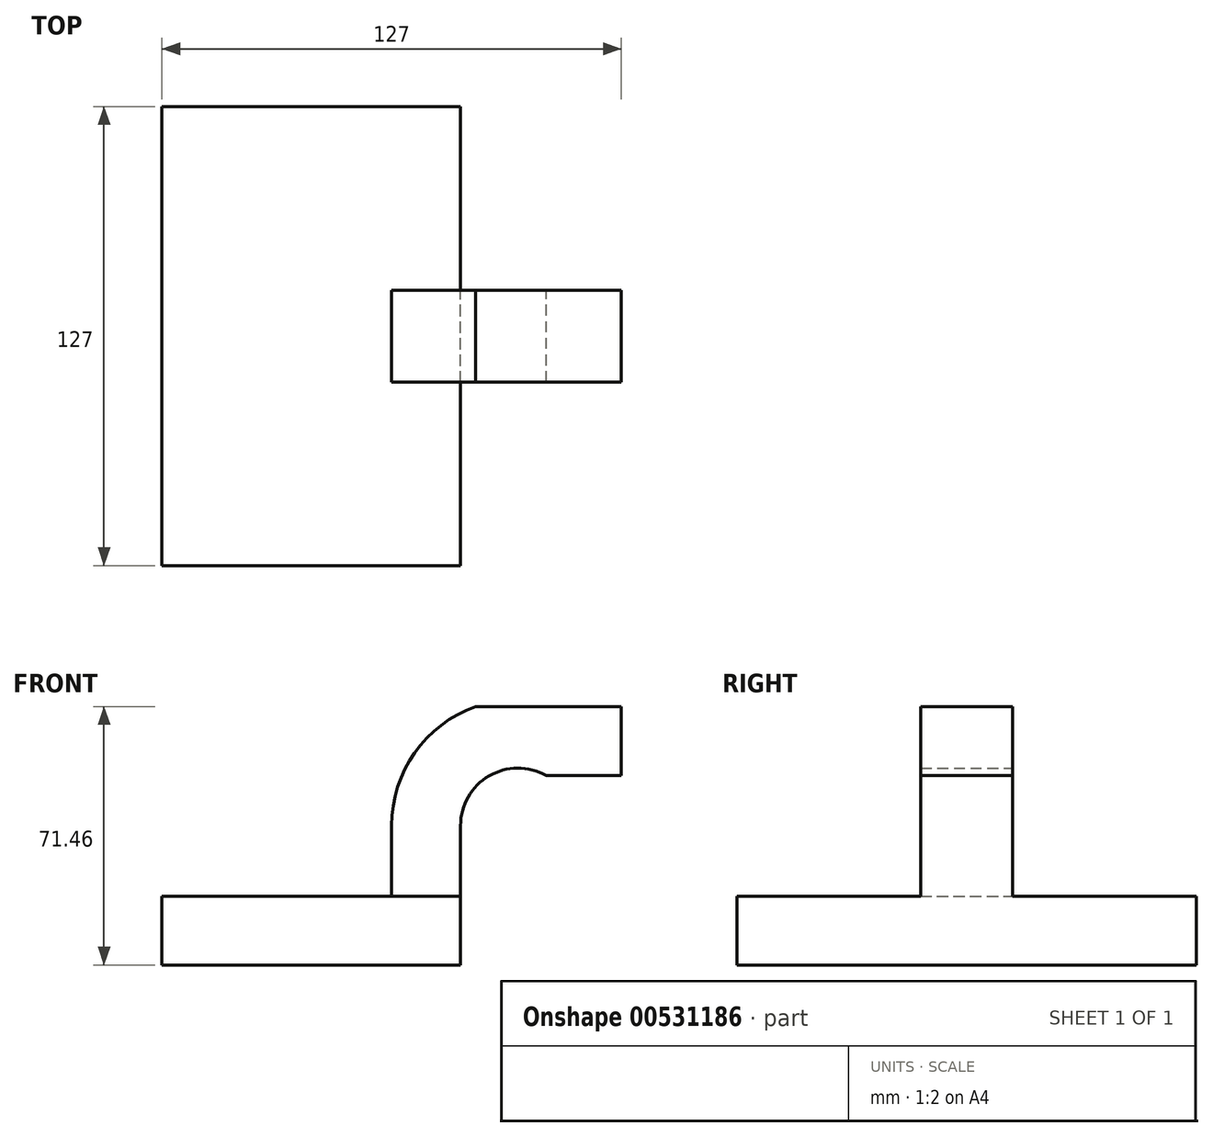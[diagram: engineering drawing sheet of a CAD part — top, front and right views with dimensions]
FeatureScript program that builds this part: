
annotation { "Feature Type Name" : "Feature", "Feature Type Description" : "" }
export const myFeature = defineFeature(function(context is Context, id is Id, definition is map)
    precondition{}
    {
        {
            var Q0;
            Q0=qCreatedBy(makeId("Front.planeOp"),FACE);
            var sketch = newSketch(context, id + "F0", { "sketchPlane" : qUnion([Q0])});
            skLineSegment(sketch, "E0.bottom", {"start": v(-41.28, -9.53) * mm, "end": v(41.28, -9.53) * mm});
            skLineSegment(sketch, "E0.top", {"start": v(-41.28, 9.53) * mm, "end": v(41.28, 9.53) * mm});
            skLineSegment(sketch, "E0.left", {"start": v(-41.28, -9.53) * mm, "end": v(-41.28, 9.53) * mm});
            skLineSegment(sketch, "E0.right", {"start": v(41.28, -9.53) * mm, "end": v(41.28, 9.53) * mm});
            skPoint(sketch, "E0.middle", {"position": v(0, 0) * mm});
            skLineSegment(sketch, "E1.bottom", {"start": v(111.12, 38.1) * mm, "end": v(60.32, 38.1) * mm});
            skLineSegment(sketch, "E1.top", {"start": v(111.12, 66.68) * mm, "end": v(60.32, 66.68) * mm});
            skLineSegment(sketch, "E1.left", {"start": v(111.12, 38.1) * mm, "end": v(111.12, 66.68) * mm});
            skLineSegment(sketch, "E1.right", {"start": v(60.32, 38.1) * mm, "end": v(60.32, 66.68) * mm});
            skPoint(sketch, "E1.middle", {"position": v(85.72, 52.39) * mm});
            skLineSegment(sketch, "E2", {"start": v(41.28, 9.53) * mm, "end": v(41.28, 29.04) * mm});
            skArc(sketch, "E3", {"start": v(41.28, 29.04) * mm, "mid": v(49.14, 42.75) * mm, "end": v(64.94, 42.88) * mm});
            skLineSegment(sketch, "E4", {"start": v(64.94, 42.88) * mm, "end": v(85.72, 42.88) * mm});
            skLineSegment(sketch, "E5.0", {"start": v(45.38, 61.93) * mm, "end": v(85.72, 61.93) * mm});
            skArc(sketch, "E5.1", {"start": v(22.23, 29.04) * mm, "mid": v(28.6, 49.15) * mm, "end": v(45.38, 61.93) * mm});
            skLineSegment(sketch, "E5.2", {"start": v(22.23, 9.53) * mm, "end": v(22.23, 29.04) * mm});
            skLineSegment(sketch, "E6", {"start": v(85.72, 38.1) * mm, "end": v(85.72, 66.68) * mm});
            skFitSpline(sketch, "E7", {"points": [v(-41.28, 9.53) * mm, v(45.38, 61.93) * mm], "startDerivative": vector(1.31, 96.4) * mm, "endDerivative": vector(180.6, -24.34) * mm});
            skSolve(sketch);
        }
        {
            var Q0;
            Q0=makeQuery(id+"F0.imprint","IMPRINT",FACE,{"disambiguationData":[TD([[makeQuery(id+"F0.imprint","IMPRINT",EDGE,{"derivedFrom":sQuery(id+"F0.wireOp",EDGE,"E0.bottom")}),1.0]])]});
            extrude(context, id + "F1", {"entities" : qUnion([Q0]), "endBound" : BoundingType.SYMMETRIC, "depth" : 127 * mm, "offsetDistance" : 25.4 * mm});
        }
        {
            var Q0;
            {var subQ1=sQuery(id+"F0.wireOp",EDGE,"E2");Q0=makeQuery(id+"F0.imprint","IMPRINT",FACE,{"disambiguationData":[TD([[makeQuery(id+"F0.imprint","IMPRINT",EDGE,{"derivedFrom":subQ1}),1.0]])]});}
            var Q1;
            {var subQ5=sQuery(id+"F0.wireOp",EDGE,"E4");Q1=makeQuery(id+"F0.imprint","IMPRINT",FACE,{"disambiguationData":[TD([[makeQuery(id+"F0.imprint","IMPRINT",EDGE,{"derivedFrom":subQ5}),1.0]])]});}
            extrude(context, id + "F2", {"entities" : qUnion([Q0, Q1]), "operationType" : NewBodyOperationType.ADD, "endBound" : BoundingType.SYMMETRIC, "depth" : 25.4 * mm, "offsetDistance" : 25.4 * mm});
        }
        {
            var Q0;
            Q0=makeQuery(id+"F0.imprint","IMPRINT",FACE,{"disambiguationData":[TD([[makeQuery(id+"F0.imprint","IMPRINT",EDGE,{"derivedFrom":sQuery(id+"F0.wireOp",EDGE,"E5.1")}),1.0]])]});
            extrude(context, id + "F3", {"entities" : qUnion([Q0]), "operationType" : NewBodyOperationType.ADD, "endBound" : BoundingType.SYMMETRIC, "depth" : 25.4 * mm, "offsetDistance" : 25.4 * mm});
        }
    });
